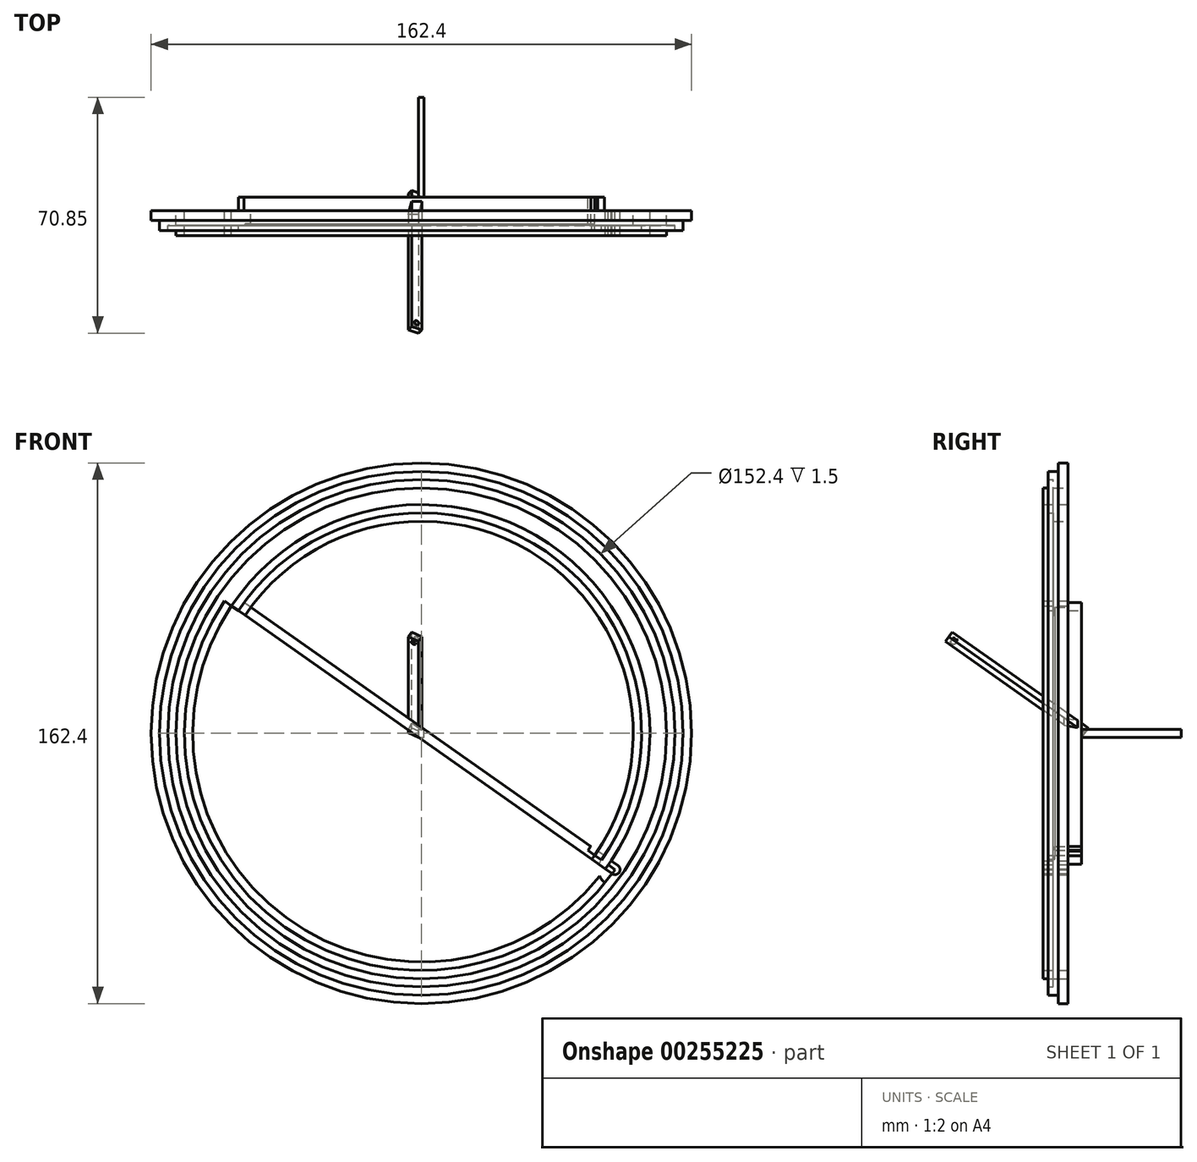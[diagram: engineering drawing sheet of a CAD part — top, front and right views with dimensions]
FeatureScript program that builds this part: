
annotation { "Feature Type Name" : "Feature", "Feature Type Description" : "" }
export const myFeature = defineFeature(function(context is Context, id is Id, definition is map)
    precondition{}
    {
        {
            var Q0;
            Q0=qCreatedBy(makeId("Front.planeOp"),FACE);
            var sketch = newSketch(context, id + "F0", { "sketchPlane" : qUnion([Q0])});
            skPoint(sketch, "E0", {"position": v(0, 0) * mm});
            skLineSegment(sketch, "E1", {"start": v(0, -2.5) * mm, "end": v(0, 2.5) * mm});
            skArc(sketch, "E2", {"start": v(0, -2.5) * mm, "mid": v(2.5, 0) * mm, "end": v(0, 2.5) * mm});
            skLineSegment(sketch, "E3", {"start": v(-25, 0) * mm, "end": v(25, 0) * mm});
            skArc(sketch, "E4", {"start": v(25, 0) * mm, "mid": v(0, 25) * mm, "end": v(-25, 0) * mm});
            skSolve(sketch);
        }
        {
            var Q0;
            Q0=qCreatedBy(makeId("Front.planeOp"),FACE);
            var sketch = newSketch(context, id + "F1", { "sketchPlane" : qUnion([Q0])});
            skLineSegment(sketch, "E5.bottom", {"start": v(51.3, 31.12) * mm, "end": v(-51.3, 31.12) * mm});
            skLineSegment(sketch, "E5.top", {"start": v(51.3, -31.12) * mm, "end": v(-51.3, -31.12) * mm});
            skLineSegment(sketch, "E5.left", {"start": v(51.3, 31.12) * mm, "end": v(51.3, -31.12) * mm});
            skLineSegment(sketch, "E5.right", {"start": v(-51.3, 31.12) * mm, "end": v(-51.3, -31.12) * mm});
            skPoint(sketch, "E5.middle", {"position": v(0, 0) * mm});
            skCircle(sketch, "E6", {"center": v(-51.3, -31.12) * mm, "radius": 2.5 * mm});
            skCircle(sketch, "E7", {"center": v(51.3, 31.12) * mm, "radius": 2.5 * mm});
            skCircle(sketch, "E8", {"center": v(51.3, 0) * mm, "radius": 2.5 * mm});
            skSolve(sketch);
        }
        {
            var Q0;
            Q0=sQuery(id+"F1.wireOp",EDGE,"E5.left");
            cPoint(context, id + "F2", {"entities" : qUnion([Q0]), "parameter" : 0.5});
        }
        {
            var Q0;
            Q0 = qCreatedBy(id + "F2" ,VERTEX);
            var Q1;
            Q1=sQuery(id+"F1.wireOp",VERTEX,"E6.center");
            var Q2;
            Q2=sQuery(id+"F0.wireOp",VERTEX,"E0");
            cPlane(context, id + "F3", {"entities" : qUnion([Q0, Q1, Q2]), "cplaneType" : CPlaneType.THREE_POINT, "offset" : 25 * mm, "width" : 150 * mm, "height" : 150 * mm});
        }
        {
            var Q0;
            Q0=qCreatedBy(id+"F3.planeOp",FACE);
            var sketch = newSketch(context, id + "F4", { "sketchPlane" : qUnion([Q0])});
            skPoint(sketch, "E9.0", {"position": v(51.3, 0) * mm});
            skPoint(sketch, "E10.0", {"position": v(0, 0) * mm});
            skEllipse(sketch, "E11.0", {"center": v(-65.18, 81.92) * mm, "majorRadius": 2.5 * mm, "minorRadius": 0.87 * mm, "majorAxis": v(-1, -0.1)});
            skPoint(sketch, "E12.0", {"position": v(-65.8, 86.24) * mm});
            skLineSegment(sketch, "E13", {"start": v(-65.18, 81.92) * mm, "end": v(51.3, 0) * mm});
            skArc(sketch, "E14", {"start": v(51.3, 0) * mm, "mid": v(-47.9, -17.28) * mm, "end": v(-65.18, 81.92) * mm});
            skArc(sketch, "E15.MirrorCS", {"start": v(51.3, 0) * mm, "mid": v(34.02, 99.2) * mm, "end": v(-65.18, 81.92) * mm});
            skArc(sketch, "E16.0.startCap", {"start": v(47.21, 2.88) * mm, "mid": v(54.18, 4.09) * mm, "end": v(55.4, -2.88) * mm, "construction": true});
            skArc(sketch, "E16.0.endCap", {"start": v(-69.27, 84.8) * mm, "mid": v(-62.3, 86) * mm, "end": v(-61.1, 79.04) * mm, "construction": true});
            skArc(sketch, "E16.0.left", {"start": v(55.4, -2.88) * mm, "mid": v(-50.78, -21.37) * mm, "end": v(-69.27, 84.8) * mm});
            skArc(sketch, "E16.0.right", {"start": v(47.21, 2.88) * mm, "mid": v(-45.02, -13.2) * mm, "end": v(-61.1, 79.04) * mm});
            skArc(sketch, "E16.1.startCap", {"start": v(55.4, -2.88) * mm, "mid": v(48.42, -4.09) * mm, "end": v(47.21, 2.88) * mm});
            skArc(sketch, "E16.1.endCap", {"start": v(-61.1, 79.04) * mm, "mid": v(-68.06, 77.83) * mm, "end": v(-69.27, 84.8) * mm, "construction": true});
            skArc(sketch, "E16.1.left", {"start": v(47.21, 2.88) * mm, "mid": v(31.14, 95.11) * mm, "end": v(-61.1, 79.04) * mm});
            skArc(sketch, "E16.1.right", {"start": v(55.4, -2.88) * mm, "mid": v(36.9, 103.29) * mm, "end": v(-69.27, 84.8) * mm});
            skArc(sketch, "E17.0.startCap", {"start": v(59.48, -5.75) * mm, "mid": v(45.55, -8.18) * mm, "end": v(43.12, 5.75) * mm, "construction": true});
            skArc(sketch, "E17.0.endCap", {"start": v(-57, 76.17) * mm, "mid": v(-70.93, 73.74) * mm, "end": v(-73.36, 87.67) * mm, "construction": true});
            skArc(sketch, "E17.0.left", {"start": v(43.12, 5.75) * mm, "mid": v(28.27, 91.02) * mm, "end": v(-57, 76.17) * mm});
            skArc(sketch, "E17.0.right", {"start": v(59.48, -5.75) * mm, "mid": v(39.77, 107.38) * mm, "end": v(-73.36, 87.67) * mm});
            skArc(sketch, "E17.1.startCap", {"start": v(43.12, 5.75) * mm, "mid": v(57.05, 8.18) * mm, "end": v(59.48, -5.75) * mm, "construction": true});
            skArc(sketch, "E17.1.endCap", {"start": v(-73.36, 87.67) * mm, "mid": v(-59.43, 90.1) * mm, "end": v(-57, 76.17) * mm, "construction": true});
            skArc(sketch, "E17.1.left", {"start": v(59.48, -5.75) * mm, "mid": v(-53.65, -25.46) * mm, "end": v(-73.36, 87.67) * mm});
            skArc(sketch, "E17.1.right", {"start": v(43.12, 5.75) * mm, "mid": v(-42.15, -9.1) * mm, "end": v(-57, 76.17) * mm});
            skArc(sketch, "E18.0.startCap", {"start": v(57.44, -4.31) * mm, "mid": v(46.99, -6.13) * mm, "end": v(45.17, 4.31) * mm, "construction": true});
            skArc(sketch, "E18.0.endCap", {"start": v(-59.05, 77.6) * mm, "mid": v(-69.5, 75.78) * mm, "end": v(-71.31, 86.23) * mm, "construction": true});
            skArc(sketch, "E18.0.left", {"start": v(45.17, 4.31) * mm, "mid": v(29.7, 93.07) * mm, "end": v(-59.05, 77.6) * mm});
            skArc(sketch, "E18.0.right", {"start": v(57.44, -4.31) * mm, "mid": v(38.33, 105.33) * mm, "end": v(-71.31, 86.23) * mm});
            skArc(sketch, "E18.1.startCap", {"start": v(45.17, 4.31) * mm, "mid": v(55.62, 6.13) * mm, "end": v(57.44, -4.31) * mm, "construction": true});
            skArc(sketch, "E18.1.endCap", {"start": v(-71.31, 86.23) * mm, "mid": v(-60.87, 88.05) * mm, "end": v(-59.05, 77.6) * mm, "construction": true});
            skArc(sketch, "E18.1.left", {"start": v(57.44, -4.31) * mm, "mid": v(-52.21, -23.42) * mm, "end": v(-71.31, 86.23) * mm});
            skArc(sketch, "E18.1.right", {"start": v(45.17, 4.31) * mm, "mid": v(-43.58, -11.15) * mm, "end": v(-59.05, 77.6) * mm});
            skArc(sketch, "E19.0.startCap", {"start": v(49.26, 1.44) * mm, "mid": v(52.74, 2.04) * mm, "end": v(53.35, -1.44) * mm, "construction": true});
            skArc(sketch, "E19.0.endCap", {"start": v(-67.22, 83.36) * mm, "mid": v(-63.74, 83.96) * mm, "end": v(-63.13, 80.48) * mm, "construction": true});
            skArc(sketch, "E19.0.left", {"start": v(53.35, -1.44) * mm, "mid": v(-49.34, -19.33) * mm, "end": v(-67.22, 83.36) * mm});
            skArc(sketch, "E19.0.right", {"start": v(49.26, 1.44) * mm, "mid": v(-46.46, -15.24) * mm, "end": v(-63.13, 80.48) * mm});
            skArc(sketch, "E19.1.startCap", {"start": v(53.35, -1.44) * mm, "mid": v(49.86, -2.04) * mm, "end": v(49.26, 1.44) * mm, "construction": true});
            skArc(sketch, "E19.1.endCap", {"start": v(-63.13, 80.48) * mm, "mid": v(-66.62, 79.87) * mm, "end": v(-67.22, 83.36) * mm, "construction": true});
            skArc(sketch, "E19.1.left", {"start": v(49.26, 1.44) * mm, "mid": v(32.58, 97.16) * mm, "end": v(-63.13, 80.48) * mm});
            skArc(sketch, "E19.1.right", {"start": v(53.35, -1.44) * mm, "mid": v(35.46, 101.25) * mm, "end": v(-67.22, 83.36) * mm});
            skArc(sketch, "E20.0.startCap", {"start": v(-66.04, 80.7) * mm, "mid": v(-66.4, 82.78) * mm, "end": v(-64.32, 83.15) * mm});
            skArc(sketch, "E20.0.endCap", {"start": v(52.16, 1.23) * mm, "mid": v(52.53, -0.86) * mm, "end": v(50.44, -1.23) * mm});
            skLineSegment(sketch, "E20.0.left", {"start": v(-64.32, 83.15) * mm, "end": v(52.16, 1.23) * mm});
            skLineSegment(sketch, "E20.0.right", {"start": v(-66.04, 80.7) * mm, "end": v(50.44, -1.23) * mm});
            skSolve(sketch);
        }
        {
            var Q0;
            Q0=makeQuery(id+"F4.imprint","IMPRINT",FACE,{"disambiguationData":[TD([[makeQuery(id+"F4.imprint","IMPRINT",EDGE,{"derivedFrom":sQuery(id+"F4.wireOp",EDGE,"E17.0.right")}),1.0]])]});
            var Q1;
            {var subQ0=sQuery(id+"F4.wireOp",EDGE,"E20.0.left");var subQ1=sQuery(id+"F4.wireOp",EDGE,"E17.0.left");var subQ2=makeQuery(id+"F4.imprint","INTERSECT",VERTEX,{"disambiguationData":[OD(0.0)],"derivedFrom":[subQ1,subQ0]});Q1=makeQuery(id+"F4.imprint","IMPRINT",FACE,{"disambiguationData":[TD([[makeQuery(id+"F4.imprint","IMPRINT",EDGE,{"disambiguationData":[TD([[subQ2,-1.0]])],"derivedFrom":subQ1}),-1.0]])]});}
            var Q2;
            {var subQ0=sQuery(id+"F4.wireOp",EDGE,"E20.0.right");var subQ1=sQuery(id+"F4.wireOp",EDGE,"E17.1.right");var subQ2=makeQuery(id+"F4.imprint","INTERSECT",VERTEX,{"disambiguationData":[OD(0.0)],"derivedFrom":[subQ1,subQ0]});Q2=makeQuery(id+"F4.imprint","IMPRINT",FACE,{"disambiguationData":[TD([[makeQuery(id+"F4.imprint","IMPRINT",EDGE,{"disambiguationData":[TD([[subQ2,-1.0]])],"derivedFrom":subQ1}),1.0]])]});}
            var Q3;
            {var subQ0=sQuery(id+"F4.wireOp",EDGE,"E17.1.right");var subQ5=sQuery(id+"F4.wireOp",EDGE,"E20.0.right");var subQ6=makeQuery(id+"F4.imprint","INTERSECT",VERTEX,{"disambiguationData":[OD(1.0)],"derivedFrom":[subQ0,subQ5]});Q3=makeQuery(id+"F4.imprint","IMPRINT",FACE,{"disambiguationData":[TD([[makeQuery(id+"F4.imprint","IMPRINT",EDGE,{"disambiguationData":[TD([[subQ6,1.0]])],"derivedFrom":subQ5}),1.0]])]});}
            var Q4;
            {var subQ0=sQuery(id+"F4.wireOp",EDGE,"E17.0.left");var subQ5=sQuery(id+"F4.wireOp",EDGE,"E20.0.left");var subQ7=makeQuery(id+"F4.imprint","INTERSECT",VERTEX,{"disambiguationData":[OD(1.0)],"derivedFrom":[subQ0,subQ5]});Q4=makeQuery(id+"F4.imprint","IMPRINT",FACE,{"disambiguationData":[TD([[makeQuery(id+"F4.imprint","IMPRINT",EDGE,{"disambiguationData":[TD([[subQ7,1.0]])],"derivedFrom":subQ5}),-1.0]])]});}
            var Q5;
            {var subQ0=sQuery(id+"F4.wireOp",EDGE,"E17.1.right");var subQ5=sQuery(id+"F4.wireOp",EDGE,"E20.0.right");var subQ6=makeQuery(id+"F4.imprint","INTERSECT",VERTEX,{"disambiguationData":[OD(0.0)],"derivedFrom":[subQ0,subQ5]});Q5=makeQuery(id+"F4.imprint","IMPRINT",FACE,{"disambiguationData":[TD([[makeQuery(id+"F4.imprint","IMPRINT",EDGE,{"disambiguationData":[TD([[subQ6,-1.0]])],"derivedFrom":subQ5}),1.0]])]});}
            var Q6;
            {var subQ0=sQuery(id+"F4.wireOp",EDGE,"E17.0.left");var subQ5=sQuery(id+"F4.wireOp",EDGE,"E20.0.left");var subQ7=makeQuery(id+"F4.imprint","INTERSECT",VERTEX,{"disambiguationData":[OD(0.0)],"derivedFrom":[subQ0,subQ5]});Q6=makeQuery(id+"F4.imprint","IMPRINT",FACE,{"disambiguationData":[TD([[makeQuery(id+"F4.imprint","IMPRINT",EDGE,{"disambiguationData":[TD([[subQ7,-1.0]])],"derivedFrom":subQ5}),-1.0]])]});}
            extrude(context, id + "F5", {"entities" : qUnion([Q0, Q1, Q2, Q3, Q4, Q5, Q6]), "depth" : 3 * mm});
        }
        {
            var Q0;
            Q0=makeQuery(id+"F4.imprint","IMPRINT",FACE,{"disambiguationData":[TD([[makeQuery(id+"F4.imprint","IMPRINT",EDGE,{"derivedFrom":sQuery(id+"F4.wireOp",EDGE,"E16.0.left")}),1.0]])]});
            var Q1;
            {var subQ0=sQuery(id+"F4.wireOp",EDGE,"E20.0.left");var subQ1=sQuery(id+"F4.wireOp",EDGE,"E16.1.left");var subQ2=makeQuery(id+"F4.imprint","INTERSECT",VERTEX,{"disambiguationData":[OD(0.0)],"derivedFrom":[subQ1,subQ0]});Q1=makeQuery(id+"F4.imprint","IMPRINT",FACE,{"disambiguationData":[TD([[makeQuery(id+"F4.imprint","IMPRINT",EDGE,{"disambiguationData":[TD([[subQ2,-1.0]])],"derivedFrom":subQ1}),1.0]])]});}
            var Q2;
            {var subQ0=sQuery(id+"F4.wireOp",EDGE,"E16.0.right");var subQ5=sQuery(id+"F4.wireOp",EDGE,"E20.0.right");var subQ6=makeQuery(id+"F4.imprint","INTERSECT",VERTEX,{"disambiguationData":[OD(1.0)],"derivedFrom":[subQ0,subQ5]});Q2=makeQuery(id+"F4.imprint","IMPRINT",FACE,{"disambiguationData":[TD([[makeQuery(id+"F4.imprint","IMPRINT",EDGE,{"disambiguationData":[TD([[subQ6,-1.0]])],"derivedFrom":subQ5}),1.0]])]});}
            var Q3;
            {var subQ0=sQuery(id+"F4.wireOp",EDGE,"E16.1.left");var subQ5=sQuery(id+"F4.wireOp",EDGE,"E20.0.left");var subQ7=makeQuery(id+"F4.imprint","INTERSECT",VERTEX,{"disambiguationData":[OD(1.0)],"derivedFrom":[subQ0,subQ5]});Q3=makeQuery(id+"F4.imprint","IMPRINT",FACE,{"disambiguationData":[TD([[makeQuery(id+"F4.imprint","IMPRINT",EDGE,{"disambiguationData":[TD([[subQ7,-1.0]])],"derivedFrom":subQ5}),-1.0]])]});}
            var Q4;
            {var subQ0=sQuery(id+"F4.wireOp",EDGE,"E20.0.right");var subQ1=sQuery(id+"F4.wireOp",EDGE,"E16.0.right");var subQ2=makeQuery(id+"F4.imprint","INTERSECT",VERTEX,{"disambiguationData":[OD(0.0)],"derivedFrom":[subQ1,subQ0]});Q4=makeQuery(id+"F4.imprint","IMPRINT",FACE,{"disambiguationData":[TD([[makeQuery(id+"F4.imprint","IMPRINT",EDGE,{"disambiguationData":[TD([[subQ2,-1.0]])],"derivedFrom":subQ1}),-1.0]])]});}
            var Q5;
            {var subQ0=sQuery(id+"F4.wireOp",EDGE,"E16.0.right");var subQ5=sQuery(id+"F4.wireOp",EDGE,"E20.0.right");var subQ6=makeQuery(id+"F4.imprint","INTERSECT",VERTEX,{"disambiguationData":[OD(0.0)],"derivedFrom":[subQ0,subQ5]});Q5=makeQuery(id+"F4.imprint","IMPRINT",FACE,{"disambiguationData":[TD([[makeQuery(id+"F4.imprint","IMPRINT",EDGE,{"disambiguationData":[TD([[subQ6,1.0]])],"derivedFrom":subQ5}),1.0]])]});}
            var Q6;
            {var subQ0=sQuery(id+"F4.wireOp",EDGE,"E16.1.left");var subQ5=sQuery(id+"F4.wireOp",EDGE,"E20.0.left");var subQ7=makeQuery(id+"F4.imprint","INTERSECT",VERTEX,{"disambiguationData":[OD(0.0)],"derivedFrom":[subQ0,subQ5]});Q6=makeQuery(id+"F4.imprint","IMPRINT",FACE,{"disambiguationData":[TD([[makeQuery(id+"F4.imprint","IMPRINT",EDGE,{"disambiguationData":[TD([[subQ7,1.0]])],"derivedFrom":subQ5}),-1.0]])]});}
            extrude(context, id + "F6", {"entities" : qUnion([Q0, Q1, Q2, Q3, Q4, Q5, Q6]), "operationType" : NewBodyOperationType.ADD, "depth" : 4.5 * mm});
        }
        {
            var Q0;
            Q0=makeQuery(id+"F4.imprint","IMPRINT",FACE,{"disambiguationData":[TD([[makeQuery(id+"F4.imprint","IMPRINT",EDGE,{"derivedFrom":sQuery(id+"F4.wireOp",EDGE,"E16.0.left")}),-1.0]])]});
            var Q1;
            {var subQ0=sQuery(id+"F4.wireOp",EDGE,"E20.0.left");var subQ1=sQuery(id+"F4.wireOp",EDGE,"E16.1.left");var subQ2=makeQuery(id+"F4.imprint","INTERSECT",VERTEX,{"disambiguationData":[OD(0.0)],"derivedFrom":[subQ1,subQ0]});Q1=makeQuery(id+"F4.imprint","IMPRINT",FACE,{"disambiguationData":[TD([[makeQuery(id+"F4.imprint","IMPRINT",EDGE,{"disambiguationData":[TD([[subQ2,-1.0]])],"derivedFrom":subQ1}),-1.0]])]});}
            var Q2;
            {var subQ0=sQuery(id+"F4.wireOp",EDGE,"E16.1.startCap");var subQ5=sQuery(id+"F4.wireOp",EDGE,"E20.0.right");var subQ6=makeQuery(id+"F4.imprint","INTERSECT",VERTEX,{"derivedFrom":[subQ0,subQ5]});Q2=makeQuery(id+"F4.imprint","IMPRINT",FACE,{"disambiguationData":[TD([[makeQuery(id+"F4.imprint","IMPRINT",EDGE,{"disambiguationData":[TD([[subQ6,-1.0]])],"derivedFrom":subQ5}),1.0]])]});}
            var Q3;
            {var subQ0=sQuery(id+"F4.wireOp",EDGE,"E16.1.left");var subQ5=sQuery(id+"F4.wireOp",EDGE,"E20.0.left");var subQ6=makeQuery(id+"F4.imprint","INTERSECT",VERTEX,{"disambiguationData":[OD(0.0)],"derivedFrom":[subQ0,subQ5]});Q3=makeQuery(id+"F4.imprint","IMPRINT",FACE,{"disambiguationData":[TD([[makeQuery(id+"F4.imprint","IMPRINT",EDGE,{"disambiguationData":[TD([[subQ6,-1.0]])],"derivedFrom":subQ5}),-1.0]])]});}
            var Q4;
            {var subQ0=sQuery(id+"F4.wireOp",EDGE,"E20.0.right");var subQ1=sQuery(id+"F4.wireOp",EDGE,"E16.0.right");var subQ8=makeQuery(id+"F4.imprint","INTERSECT",VERTEX,{"disambiguationData":[OD(0.0)],"derivedFrom":[subQ1,subQ0]});Q4=makeQuery(id+"F4.imprint","IMPRINT",FACE,{"disambiguationData":[TD([[makeQuery(id+"F4.imprint","IMPRINT",EDGE,{"disambiguationData":[TD([[subQ8,-1.0]])],"derivedFrom":subQ1}),1.0]])]});}
            var Q5;
            {var subQ0=sQuery(id+"F4.wireOp",EDGE,"E19.0.right");var subQ1=sQuery(id+"F4.wireOp",EDGE,"E16.1.startCap");var subQ2=makeQuery(id+"F4.imprint","INTERSECT",VERTEX,{"derivedFrom":[subQ1,subQ0]});Q5=makeQuery(id+"F4.imprint","IMPRINT",FACE,{"disambiguationData":[TD([[makeQuery(id+"F4.imprint","IMPRINT",EDGE,{"disambiguationData":[TD([[subQ2,-1.0]])],"derivedFrom":subQ1}),-1.0]])]});}
            var Q6;
            {var subQ1=sQuery(id+"F4.wireOp",EDGE,"E16.0.right");var subQ3=sQuery(id+"F4.wireOp",EDGE,"E20.0.right");var subQ4=makeQuery(id+"F4.imprint","INTERSECT",VERTEX,{"disambiguationData":[OD(0.0)],"derivedFrom":[subQ1,subQ3]});Q6=makeQuery(id+"F4.imprint","IMPRINT",FACE,{"disambiguationData":[TD([[makeQuery(id+"F4.imprint","IMPRINT",EDGE,{"disambiguationData":[TD([[subQ4,-1.0]])],"derivedFrom":subQ3}),1.0]])]});}
            var Q7;
            {var subQ0=sQuery(id+"F4.wireOp",EDGE,"E16.1.left");var subQ5=sQuery(id+"F4.wireOp",EDGE,"E20.0.left");var subQ6=makeQuery(id+"F4.imprint","INTERSECT",VERTEX,{"disambiguationData":[OD(1.0)],"derivedFrom":[subQ0,subQ5]});Q7=makeQuery(id+"F4.imprint","IMPRINT",FACE,{"disambiguationData":[TD([[makeQuery(id+"F4.imprint","IMPRINT",EDGE,{"disambiguationData":[TD([[subQ6,1.0]])],"derivedFrom":subQ5}),-1.0]])]});}
            var Q8;
            {var subQ0=sQuery(id+"F4.wireOp",EDGE,"E16.0.right");var subQ5=sQuery(id+"F4.wireOp",EDGE,"E20.0.right");var subQ6=makeQuery(id+"F4.imprint","INTERSECT",VERTEX,{"disambiguationData":[OD(1.0)],"derivedFrom":[subQ0,subQ5]});Q8=makeQuery(id+"F4.imprint","IMPRINT",FACE,{"disambiguationData":[TD([[makeQuery(id+"F4.imprint","IMPRINT",EDGE,{"disambiguationData":[TD([[subQ6,1.0]])],"derivedFrom":subQ5}),1.0]])]});}
            extrude(context, id + "F7", {"entities" : qUnion([Q0, Q1, Q2, Q3, Q4, Q5, Q6, Q7, Q8]), "operationType" : NewBodyOperationType.ADD, "depth" : 6 * mm});
        }
        {
            var Q0;
            {var subQ0=sQuery(id+"F4.wireOp",EDGE,"E16.1.startCap");var subQ1=sQuery(id+"F4.wireOp",EDGE,"E14");var subQ2=makeQuery(id+"F4.imprint","INTERSECT",VERTEX,{"derivedFrom":[subQ1,subQ0]});Q0=makeQuery(id+"F4.imprint","IMPRINT",FACE,{"disambiguationData":[TD([[makeQuery(id+"F4.imprint","IMPRINT",EDGE,{"disambiguationData":[TD([[subQ2,-1.0]])],"derivedFrom":subQ1}),-1.0]])]});}
            var Q1;
            {var subQ9=sQuery(id+"F4.wireOp",EDGE,"E19.1.right");Q1=makeQuery(id+"F4.imprint","IMPRINT",FACE,{"disambiguationData":[TD([[makeQuery(id+"F4.imprint","IMPRINT",EDGE,{"derivedFrom":subQ9}),1.0]])]});}
            var Q2;
            {var subQ0=sQuery(id+"F4.wireOp",EDGE,"E20.0.startCap");var subQ1=sQuery(id+"F4.wireOp",EDGE,"E11.0");var subQ2=makeQuery(id+"F4.imprint","INTERSECT",VERTEX,{"disambiguationData":[OD(0.0)],"derivedFrom":[subQ1,subQ0]});Q2=makeQuery(id+"F4.imprint","IMPRINT",FACE,{"disambiguationData":[TD([[makeQuery(id+"F4.imprint","IMPRINT",EDGE,{"disambiguationData":[TD([[subQ2,1.0]])],"derivedFrom":subQ1}),1.0]])]});}
            var Q3;
            {var subQ1=sQuery(id+"F4.wireOp",EDGE,"E14");var subQ3=sQuery(id+"F4.wireOp",EDGE,"E11.0");var subQ5=makeQuery(id+"F4.imprint","INTERSECT",VERTEX,{"derivedFrom":[subQ3,subQ1]});Q3=makeQuery(id+"F4.imprint","IMPRINT",FACE,{"disambiguationData":[TD([[makeQuery(id+"F4.imprint","IMPRINT",EDGE,{"disambiguationData":[TD([[subQ5,1.0]])],"derivedFrom":subQ3}),1.0]])]});}
            var Q4;
            {var subQ0=sQuery(id+"F4.wireOp",EDGE,"E14");var subQ1=sQuery(id+"F4.wireOp",EDGE,"E11.0");var subQ2=makeQuery(id+"F4.imprint","INTERSECT",VERTEX,{"derivedFrom":[subQ1,subQ0]});Q4=makeQuery(id+"F4.imprint","IMPRINT",FACE,{"disambiguationData":[TD([[makeQuery(id+"F4.imprint","IMPRINT",EDGE,{"disambiguationData":[TD([[subQ2,1.0]])],"derivedFrom":subQ1}),-1.0]])]});}
            var Q5;
            {var subQ0=sQuery(id+"F4.wireOp",EDGE,"E15.MirrorCS");var subQ1=sQuery(id+"F4.wireOp",EDGE,"E11.0");var subQ2=makeQuery(id+"F4.imprint","INTERSECT",VERTEX,{"derivedFrom":[subQ1,subQ0]});Q5=makeQuery(id+"F4.imprint","IMPRINT",FACE,{"disambiguationData":[TD([[makeQuery(id+"F4.imprint","IMPRINT",EDGE,{"disambiguationData":[TD([[subQ2,-1.0]])],"derivedFrom":subQ1}),-1.0]])]});}
            var Q6;
            {var subQ0=sQuery(id+"F4.wireOp",EDGE,"E20.0.left");var subQ1=sQuery(id+"F4.wireOp",EDGE,"E11.0");var subQ2=makeQuery(id+"F4.imprint","INTERSECT",VERTEX,{"disambiguationData":[OD(1.0)],"derivedFrom":[subQ1,subQ0]});Q6=makeQuery(id+"F4.imprint","IMPRINT",FACE,{"disambiguationData":[TD([[makeQuery(id+"F4.imprint","IMPRINT",EDGE,{"disambiguationData":[TD([[subQ2,-1.0]])],"derivedFrom":subQ1}),-1.0]])]});}
            var Q7;
            {var subQ0=sQuery(id+"F4.wireOp",EDGE,"E14");var subQ1=sQuery(id+"F4.wireOp",EDGE,"E11.0");var subQ2=makeQuery(id+"F4.imprint","INTERSECT",VERTEX,{"derivedFrom":[subQ1,subQ0]});Q7=makeQuery(id+"F4.imprint","IMPRINT",FACE,{"disambiguationData":[TD([[makeQuery(id+"F4.imprint","IMPRINT",EDGE,{"disambiguationData":[TD([[subQ2,-1.0]])],"derivedFrom":subQ1}),1.0]])]});}
            var Q8;
            {var subQ5=sQuery(id+"F4.wireOp",EDGE,"E14");var subQ6=sQuery(id+"F4.wireOp",EDGE,"E11.0");var subQ7=makeQuery(id+"F4.imprint","INTERSECT",VERTEX,{"derivedFrom":[subQ6,subQ5]});Q8=makeQuery(id+"F4.imprint","IMPRINT",FACE,{"disambiguationData":[TD([[makeQuery(id+"F4.imprint","IMPRINT",EDGE,{"disambiguationData":[TD([[subQ7,-1.0]])],"derivedFrom":subQ6}),-1.0]])]});}
            var Q9;
            {var subQ0=sQuery(id+"F4.wireOp",EDGE,"E13");var subQ1=sQuery(id+"F4.wireOp",EDGE,"E11.0");var subQ2=makeQuery(id+"F4.imprint","INTERSECT",VERTEX,{"derivedFrom":[subQ1,subQ0]});Q9=makeQuery(id+"F4.imprint","IMPRINT",FACE,{"disambiguationData":[TD([[makeQuery(id+"F4.imprint","IMPRINT",EDGE,{"disambiguationData":[TD([[subQ2,-1.0]])],"derivedFrom":subQ1}),-1.0]])]});}
            var Q10;
            {var subQ0=sQuery(id+"F4.wireOp",EDGE,"E20.0.left");var subQ1=sQuery(id+"F4.wireOp",EDGE,"E11.0");var subQ9=makeQuery(id+"F4.imprint","INTERSECT",VERTEX,{"disambiguationData":[OD(0.0)],"derivedFrom":[subQ1,subQ0]});Q10=makeQuery(id+"F4.imprint","IMPRINT",FACE,{"disambiguationData":[TD([[makeQuery(id+"F4.imprint","IMPRINT",EDGE,{"disambiguationData":[TD([[subQ9,-1.0]])],"derivedFrom":subQ1}),-1.0]])]});}
            var Q11;
            {var subQ0=sQuery(id+"F4.wireOp",EDGE,"E20.0.left");var subQ1=sQuery(id+"F4.wireOp",EDGE,"E11.0");var subQ2=makeQuery(id+"F4.imprint","INTERSECT",VERTEX,{"disambiguationData":[OD(0.0)],"derivedFrom":[subQ1,subQ0]});Q11=makeQuery(id+"F4.imprint","IMPRINT",FACE,{"disambiguationData":[TD([[makeQuery(id+"F4.imprint","IMPRINT",EDGE,{"disambiguationData":[TD([[subQ2,-1.0]])],"derivedFrom":subQ1}),1.0]])]});}
            var Q12;
            {var subQ1=sQuery(id+"F4.wireOp",EDGE,"E13");var subQ3=sQuery(id+"F4.wireOp",EDGE,"E11.0");var subQ7=makeQuery(id+"F4.imprint","INTERSECT",VERTEX,{"derivedFrom":[subQ3,subQ1]});Q12=makeQuery(id+"F4.imprint","IMPRINT",FACE,{"disambiguationData":[TD([[makeQuery(id+"F4.imprint","IMPRINT",EDGE,{"disambiguationData":[TD([[subQ7,-1.0]])],"derivedFrom":subQ3}),1.0]])]});}
            var Q13;
            {var subQ0=sQuery(id+"F4.wireOp",EDGE,"E16.1.startCap");var subQ1=sQuery(id+"F4.wireOp",EDGE,"E14");var subQ2=makeQuery(id+"F4.imprint","INTERSECT",VERTEX,{"derivedFrom":[subQ1,subQ0]});Q13=makeQuery(id+"F4.imprint","IMPRINT",FACE,{"disambiguationData":[TD([[makeQuery(id+"F4.imprint","IMPRINT",EDGE,{"disambiguationData":[TD([[subQ2,1.0]])],"derivedFrom":subQ1}),-1.0]])]});}
            var Q14;
            {var subQ0=sQuery(id+"F4.wireOp",EDGE,"E14");var subQ5=sQuery(id+"F4.wireOp",EDGE,"E20.0.right");var subQ6=makeQuery(id+"F4.imprint","INTERSECT",VERTEX,{"disambiguationData":[OD(0.0)],"derivedFrom":[subQ0,subQ5]});Q14=makeQuery(id+"F4.imprint","IMPRINT",FACE,{"disambiguationData":[TD([[makeQuery(id+"F4.imprint","IMPRINT",EDGE,{"disambiguationData":[TD([[subQ6,1.0]])],"derivedFrom":subQ5}),1.0]])]});}
            var Q15;
            {var subQ1=sQuery(id+"F4.wireOp",EDGE,"E20.0.endCap");Q15=makeQuery(id+"F4.imprint","IMPRINT",FACE,{"disambiguationData":[TD([[makeQuery(id+"F4.imprint","IMPRINT",EDGE,{"derivedFrom":subQ1}),-1.0]])]});}
            var Q16;
            {var subQ0=sQuery(id+"F4.wireOp",EDGE,"E15.MirrorCS");var subQ5=sQuery(id+"F4.wireOp",EDGE,"E20.0.left");var subQ6=makeQuery(id+"F4.imprint","INTERSECT",VERTEX,{"disambiguationData":[OD(0.0)],"derivedFrom":[subQ0,subQ5]});Q16=makeQuery(id+"F4.imprint","IMPRINT",FACE,{"disambiguationData":[TD([[makeQuery(id+"F4.imprint","IMPRINT",EDGE,{"disambiguationData":[TD([[subQ6,1.0]])],"derivedFrom":subQ5}),-1.0]])]});}
            extrude(context, id + "F8", {"entities" : qUnion([Q0, Q1, Q2, Q3, Q4, Q5, Q6, Q7, Q8, Q9, Q10, Q11, Q12, Q13, Q14, Q15, Q16]), "depth" : 7.5 * mm});
        }
        {
            var Q0;
            {var subQ1=sQuery(id+"F4.wireOp",EDGE,"E17.0.left");var subQ5=sQuery(id+"F4.wireOp",EDGE,"E20.0.left");var subQ6=makeQuery(id+"F4.imprint","INTERSECT",VERTEX,{"disambiguationData":[OD(0.0)],"derivedFrom":[subQ1,subQ5]});Q0=makeQuery(id+"F4.imprint","IMPRINT",FACE,{"disambiguationData":[TD([[makeQuery(id+"F4.imprint","IMPRINT",EDGE,{"disambiguationData":[TD([[subQ6,1.0]])],"derivedFrom":subQ5}),-1.0]])]});}
            var Q1;
            {var subQ0=sQuery(id+"F4.wireOp",EDGE,"E17.1.right");var subQ5=sQuery(id+"F4.wireOp",EDGE,"E20.0.right");var subQ7=makeQuery(id+"F4.imprint","INTERSECT",VERTEX,{"disambiguationData":[OD(0.0)],"derivedFrom":[subQ0,subQ5]});Q1=makeQuery(id+"F4.imprint","IMPRINT",FACE,{"disambiguationData":[TD([[makeQuery(id+"F4.imprint","IMPRINT",EDGE,{"disambiguationData":[TD([[subQ7,1.0]])],"derivedFrom":subQ5}),1.0]])]});}
            var Q2;
            {var subQ0=sQuery(id+"F4.wireOp",EDGE,"E16.0.right");var subQ5=sQuery(id+"F4.wireOp",EDGE,"E20.0.right");var subQ6=makeQuery(id+"F4.imprint","INTERSECT",VERTEX,{"disambiguationData":[OD(0.0)],"derivedFrom":[subQ0,subQ5]});Q2=makeQuery(id+"F4.imprint","IMPRINT",FACE,{"disambiguationData":[TD([[makeQuery(id+"F4.imprint","IMPRINT",EDGE,{"disambiguationData":[TD([[subQ6,1.0]])],"derivedFrom":subQ5}),1.0]])]});}
            var Q3;
            {var subQ0=sQuery(id+"F4.wireOp",EDGE,"E17.1.right");var subQ5=sQuery(id+"F4.wireOp",EDGE,"E20.0.right");var subQ7=makeQuery(id+"F4.imprint","INTERSECT",VERTEX,{"disambiguationData":[OD(0.0)],"derivedFrom":[subQ0,subQ5]});Q3=makeQuery(id+"F4.imprint","IMPRINT",FACE,{"disambiguationData":[TD([[makeQuery(id+"F4.imprint","IMPRINT",EDGE,{"disambiguationData":[TD([[subQ7,-1.0]])],"derivedFrom":subQ5}),1.0]])]});}
            var Q4;
            {var subQ0=sQuery(id+"F4.wireOp",EDGE,"E17.0.left");var subQ5=sQuery(id+"F4.wireOp",EDGE,"E20.0.left");var subQ7=makeQuery(id+"F4.imprint","INTERSECT",VERTEX,{"disambiguationData":[OD(0.0)],"derivedFrom":[subQ0,subQ5]});Q4=makeQuery(id+"F4.imprint","IMPRINT",FACE,{"disambiguationData":[TD([[makeQuery(id+"F4.imprint","IMPRINT",EDGE,{"disambiguationData":[TD([[subQ7,-1.0]])],"derivedFrom":subQ5}),-1.0]])]});}
            var Q5;
            {var subQ0=sQuery(id+"F4.wireOp",EDGE,"E16.1.left");var subQ5=sQuery(id+"F4.wireOp",EDGE,"E20.0.left");var subQ6=makeQuery(id+"F4.imprint","INTERSECT",VERTEX,{"disambiguationData":[OD(0.0)],"derivedFrom":[subQ0,subQ5]});Q5=makeQuery(id+"F4.imprint","IMPRINT",FACE,{"disambiguationData":[TD([[makeQuery(id+"F4.imprint","IMPRINT",EDGE,{"disambiguationData":[TD([[subQ6,1.0]])],"derivedFrom":subQ5}),-1.0]])]});}
            var Q6;
            {var subQ0=sQuery(id+"F4.wireOp",EDGE,"E17.0.left");var subQ5=sQuery(id+"F4.wireOp",EDGE,"E20.0.left");var subQ6=makeQuery(id+"F4.imprint","INTERSECT",VERTEX,{"disambiguationData":[OD(1.0)],"derivedFrom":[subQ0,subQ5]});Q6=makeQuery(id+"F4.imprint","IMPRINT",FACE,{"disambiguationData":[TD([[makeQuery(id+"F4.imprint","IMPRINT",EDGE,{"disambiguationData":[TD([[subQ6,1.0]])],"derivedFrom":subQ5}),-1.0]])]});}
            var Q7;
            {var subQ0=sQuery(id+"F4.wireOp",EDGE,"E17.1.right");var subQ5=sQuery(id+"F4.wireOp",EDGE,"E20.0.right");var subQ6=makeQuery(id+"F4.imprint","INTERSECT",VERTEX,{"disambiguationData":[OD(1.0)],"derivedFrom":[subQ0,subQ5]});Q7=makeQuery(id+"F4.imprint","IMPRINT",FACE,{"disambiguationData":[TD([[makeQuery(id+"F4.imprint","IMPRINT",EDGE,{"disambiguationData":[TD([[subQ6,1.0]])],"derivedFrom":subQ5}),1.0]])]});}
            var Q8;
            {var subQ0=sQuery(id+"F4.wireOp",EDGE,"E16.1.left");var subQ5=sQuery(id+"F4.wireOp",EDGE,"E20.0.left");var subQ6=makeQuery(id+"F4.imprint","INTERSECT",VERTEX,{"disambiguationData":[OD(1.0)],"derivedFrom":[subQ0,subQ5]});Q8=makeQuery(id+"F4.imprint","IMPRINT",FACE,{"disambiguationData":[TD([[makeQuery(id+"F4.imprint","IMPRINT",EDGE,{"disambiguationData":[TD([[subQ6,-1.0]])],"derivedFrom":subQ5}),-1.0]])]});}
            var Q9;
            {var subQ0=sQuery(id+"F4.wireOp",EDGE,"E16.0.right");var subQ5=sQuery(id+"F4.wireOp",EDGE,"E20.0.right");var subQ6=makeQuery(id+"F4.imprint","INTERSECT",VERTEX,{"disambiguationData":[OD(1.0)],"derivedFrom":[subQ0,subQ5]});Q9=makeQuery(id+"F4.imprint","IMPRINT",FACE,{"disambiguationData":[TD([[makeQuery(id+"F4.imprint","IMPRINT",EDGE,{"disambiguationData":[TD([[subQ6,-1.0]])],"derivedFrom":subQ5}),1.0]])]});}
            extrude(context, id + "F9", {"entities" : qUnion([Q0, Q1, Q2, Q3, Q4, Q5, Q6, Q7, Q8, Q9]), "endBound" : BoundingType.SYMMETRIC, "depth" : 8 * mm});
        }
        {
            var Q0;
            {var subQ0=sQuery(id+"F4.wireOp",EDGE,"E20.0.right");var subQ1=sQuery(id+"F4.wireOp",EDGE,"E17.1.right");var subQ2=makeQuery(id+"F4.imprint","INTERSECT",VERTEX,{"disambiguationData":[OD(0.0)],"derivedFrom":[subQ1,subQ0]});Q0=makeQuery(id+"F4.imprint","IMPRINT",FACE,{"disambiguationData":[TD([[makeQuery(id+"F4.imprint","IMPRINT",EDGE,{"disambiguationData":[TD([[subQ2,-1.0]])],"derivedFrom":subQ1}),-1.0]])]});}
            var sketch = newSketch(context, id + "F10", { "sketchPlane" : qUnion([Q0])});
            skPoint(sketch, "E21.0", {"position": v(-6.94, 40.96) * mm});
            skLineSegment(sketch, "E22", {"start": v(-48.32, 36.06) * mm, "end": v(34.44, 45.86) * mm});
            skArc(sketch, "E23", {"start": v(-48.36, 36.06) * mm, "mid": v(-2.08, -0.43) * mm, "end": v(34.41, 45.85) * mm});
            skLineSegment(sketch, "E24", {"start": v(-6.94, 40.96) * mm, "end": v(-2.08, -0.43) * mm});
            skLineSegment(sketch, "E25", {"start": v(-6.94, 40.96) * mm, "end": v(-32.77, 8.23) * mm});
            skLineSegment(sketch, "E26", {"start": v(-6.94, 40.96) * mm, "end": v(-43.32, 20.57) * mm});
            skArc(sketch, "E27", {"start": v(-41.76, 18.01) * mm, "mid": v(-40.7, 22.04) * mm, "end": v(-44.7, 23.24) * mm});
            skSolve(sketch);
        }
        {
            var Q0;
            Q0=sQuery(id+"F10.wireOp",EDGE,"E23");
            var Q1;
            Q1=sQuery(id+"F10.wireOp",EDGE,"E22");
            revolve(context, id + "F11", {"bodyType" : ToolBodyType.SURFACE, "surfaceEntities" : qUnion([Q0]), "axis" : qUnion([Q1]), "revolveType" : RevolveType.FULL});
        }
        {
            var Q0;
            Q0=makeQuery(id+"F9.opExtrude","CAP_FACE",FACE,{"disambiguationData":[OSD([sQuery(id+"F4.wireOp",EDGE,"E16.0.right"),sQuery(id+"F4.wireOp",EDGE,"E16.1.left"),sQuery(id+"F4.wireOp",EDGE,"E20.0.left"),sQuery(id+"F4.wireOp",EDGE,"E20.0.right")])],"isStart":true});
            var sketch = newSketch(context, id + "F12", { "sketchPlane" : qUnion([Q0])});
            skLineSegment(sketch, "E28.bottom", {"start": v(7.8, 39.73) * mm, "end": v(6.08, 39.73) * mm});
            skLineSegment(sketch, "E28.top", {"start": v(7.8, 42.19) * mm, "end": v(6.08, 42.19) * mm});
            skLineSegment(sketch, "E28.left", {"start": v(7.8, 39.73) * mm, "end": v(7.8, 42.19) * mm});
            skLineSegment(sketch, "E28.right", {"start": v(6.08, 39.73) * mm, "end": v(6.08, 42.19) * mm});
            skPoint(sketch, "E28.middle", {"position": v(6.94, 40.96) * mm});
            skSolve(sketch);
        }
        {
            var Q0;
            Q0 = qSketchRegion(id + "F12", true);
            extrude(context, id + "F13", {"entities" : qUnion([Q0]), "operationType" : NewBodyOperationType.ADD, "depth" : 30 * mm});
        }
        {
            var Q0;
            {var subQ0=sQuery(id+"F4.wireOp",EDGE,"E20.0.right");var subQ1=sQuery(id+"F4.wireOp",EDGE,"E16.1.left");var subQ2=sQuery(id+"F4.wireOp",EDGE,"E16.0.right");var subQ4=sQuery(id+"F4.wireOp",EDGE,"E20.0.left");Q0=makeQuery(id+"F13.boolean.opBoolean","SPLIT",EDGE,{"disambiguationData":[TD([makeQuery(id+"F9.opExtrude","SWEPT_FACE",FACE,{"disambiguationData":[OSD([subQ2,subQ1]),TDD([makeQuery(id+"F4.imprint","IMPRINT",EDGE,{"disambiguationData":[TD([[makeQuery(id+"F4.imprint","INTERSECT",VERTEX,{"disambiguationData":[OD(1.0)],"derivedFrom":[subQ2,subQ0]}),-1.0]])],"derivedFrom":subQ2}),makeQuery(id+"F4.imprint","IMPRINT",EDGE,{"disambiguationData":[TD([[makeQuery(id+"F4.imprint","INTERSECT",VERTEX,{"disambiguationData":[OD(1.0)],"derivedFrom":[subQ1,subQ4]}),-1.0]])],"derivedFrom":subQ1})])]})])],"derivedFrom":makeQuery(id+"F9.opExtrude","CAP_EDGE",EDGE,{"disambiguationData":[OSD([subQ0])],"isStart":true})});}
            var Q1;
            Q1=makeQuery(id+"F13.opExtrude","SWEPT_EDGE",EDGE,{"disambiguationData":[OSD([sQuery(id+"F4.wireOp",EDGE,"E20.0.right"),sQuery(id+"F12.wireOp",EDGE,"E28.bottom"),sQuery(id+"F12.wireOp",EDGE,"E28.left")])]});
            cPlane(context, id + "F14", {"entities" : qUnion([Q0, Q1]), "cplaneType" : CPlaneType.LINE_ANGLE, "offset" : 25 * mm, "angle" : (5 * PI / 6) * radian, "width" : 150 * mm, "height" : 150 * mm});
        }
        {
            var Q0;
            Q0=qCreatedBy(id+"F14.planeOp",FACE);
            var sketch = newSketch(context, id + "F15", { "sketchPlane" : qUnion([Q0])});
            skPoint(sketch, "E29.0", {"position": v(-24.09, -19.64) * mm});
            skLineSegment(sketch, "E30", {"start": v(-24.09, -19.64) * mm, "end": v(-27.59, -19.64) * mm});
            skLineSegment(sketch, "E31", {"start": v(-27.59, -19.64) * mm, "end": v(-27.59, -69.64) * mm});
            skLineSegment(sketch, "E32", {"start": v(-24.09, -19.64) * mm, "end": v(-24.09, -69.64) * mm});
            skLineSegment(sketch, "E33", {"start": v(-24.09, -69.64) * mm, "end": v(-27.59, -69.64) * mm});
            skSolve(sketch);
        }
        {
            var Q0;
            Q0=makeQuery(id+"F15.imprint","IMPRINT",FACE,{"disambiguationData":[TD([[makeQuery(id+"F15.imprint","IMPRINT",EDGE,{"derivedFrom":sQuery(id+"F15.wireOp",EDGE,"E30")}),1.0]])]});
            extrude(context, id + "F16", {"entities" : qUnion([Q0]), "operationType" : NewBodyOperationType.ADD, "depth" : 2 * mm});
        }
        {
            var Q0;
            {var subQ0=sQuery(id+"F15.wireOp",EDGE,"E32");var subQ1=sQuery(id+"F15.wireOp",EDGE,"E31");var subQ2=sQuery(id+"F15.wireOp",EDGE,"E33");Q0=makeQuery(id+"F16.boolean.opBoolean","SPLIT",FACE,{"disambiguationData":[TD([makeQuery(id+"F9.opExtrude","SWEPT_FACE",FACE,{"disambiguationData":[OSD([sQuery(id+"F4.wireOp",EDGE,"E20.0.left")])]})])],"derivedFrom":makeQuery(id+"F16.opExtrude","CAP_FACE",FACE,{"disambiguationData":[OSD([sQuery(id+"F15.wireOp",EDGE,"E30"),subQ1,subQ0,subQ2])],"isStart":true})});}
            var sketch = newSketch(context, id + "F17", { "sketchPlane" : qUnion([Q0])});
            skPoint(sketch, "E34", {"position": v(-25.84, 67.64) * mm});
            skPoint(sketch, "E34.positionSnap0", {"position": v(-25.84, 69.64) * mm});
            skCircle(sketch, "E35", {"center": v(-25.84, 67.64) * mm, "radius": 0.73 * mm});
            skSolve(sketch);
        }
        {
            var Q0;
            Q0 = qSketchRegion(id + "F17", true);
            var Q1;
            {var subQ0=sQuery(id+"F15.wireOp",EDGE,"E32");var subQ1=sQuery(id+"F15.wireOp",EDGE,"E31");var subQ2=sQuery(id+"F15.wireOp",EDGE,"E33");Q1=makeQuery(id+"F16.boolean.opBoolean","SPLIT",FACE,{"disambiguationData":[TD([makeQuery(id+"F9.opExtrude","SWEPT_FACE",FACE,{"disambiguationData":[OSD([sQuery(id+"F4.wireOp",EDGE,"E20.0.left")])]})])],"derivedFrom":makeQuery(id+"F16.opExtrude","CAP_FACE",FACE,{"disambiguationData":[OSD([sQuery(id+"F15.wireOp",EDGE,"E30"),subQ1,subQ0,subQ2])],"isStart":false})});}
            extrude(context, id + "F18", {"entities" : qUnion([Q0]), "operationType" : NewBodyOperationType.REMOVE, "endBound" : BoundingType.UP_TO_SURFACE, "oppositeDirection" : true, "endBoundEntityFace" : qUnion([Q1]), "depth" : 25 * mm});
        }
    });
